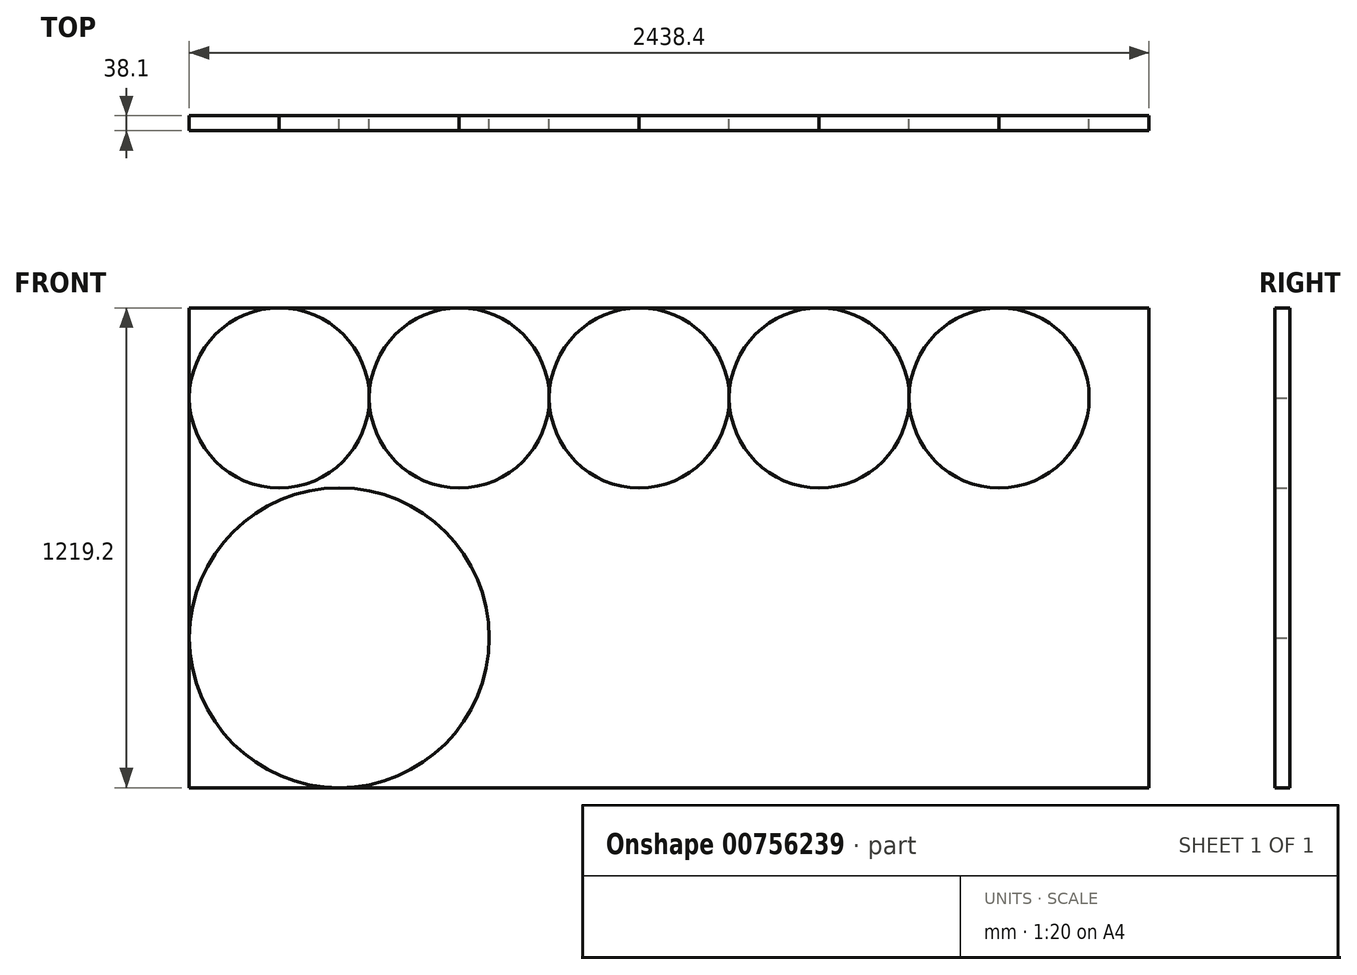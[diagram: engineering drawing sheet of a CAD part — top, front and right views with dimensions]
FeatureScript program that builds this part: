
annotation { "Feature Type Name" : "Feature", "Feature Type Description" : "" }
export const myFeature = defineFeature(function(context is Context, id is Id, definition is map)
    precondition{}
    {
        {
            var Q0;
            Q0=qCreatedBy(makeId("Front.planeOp"),FACE);
            var sketch = newSketch(context, id + "F0", { "sketchPlane" : qUnion([Q0])});
            skLineSegment(sketch, "E0.bottom", {"start": v(-1219.2, 609.6) * mm, "end": v(1219.2, 609.6) * mm});
            skLineSegment(sketch, "E0.top", {"start": v(-1219.2, -609.6) * mm, "end": v(1219.2, -609.6) * mm});
            skLineSegment(sketch, "E0.left", {"start": v(-1219.2, 609.6) * mm, "end": v(-1219.2, -609.6) * mm});
            skLineSegment(sketch, "E0.right", {"start": v(1219.2, 609.6) * mm, "end": v(1219.2, -609.6) * mm});
            skPoint(sketch, "E0.middle", {"position": v(0, 0) * mm});
            skCircle(sketch, "E1", {"center": v(-990.6, 381) * mm, "radius": 228.6 * mm});
            skCircle(sketch, "E2", {"center": v(-533.4, 381) * mm, "radius": 228.6 * mm});
            skCircle(sketch, "E3", {"center": v(-76.2, 381) * mm, "radius": 228.6 * mm});
            skCircle(sketch, "E4", {"center": v(381, 381) * mm, "radius": 228.6 * mm});
            skCircle(sketch, "E5", {"center": v(838.2, 381) * mm, "radius": 228.6 * mm});
            skCircle(sketch, "E6", {"center": v(-838.2, -228.6) * mm, "radius": 381 * mm});
            skSolve(sketch);
        }
        {
            var Q0;
            {var subQ0=sQuery(id+"F0.wireOp",EDGE,"E0.left");var subQ1=sQuery(id+"F0.wireOp",EDGE,"E0.bottom");var subQ2=makeQuery(id+"F0.imprint","INTERSECT",VERTEX,{"derivedFrom":[subQ1,subQ0]});Q0=makeQuery(id+"F0.imprint","IMPRINT",FACE,{"disambiguationData":[TD([[makeQuery(id+"F0.imprint","IMPRINT",EDGE,{"disambiguationData":[TD([[subQ2,-1.0]])],"derivedFrom":subQ1}),-1.0]])]});}
            var Q1;
            {var subQ0=sQuery(id+"F0.wireOp",EDGE,"E1");var subQ1=sQuery(id+"F0.wireOp",EDGE,"E0.bottom");var subQ2=makeQuery(id+"F0.imprint","INTERSECT",VERTEX,{"derivedFrom":[subQ1,subQ0]});Q1=makeQuery(id+"F0.imprint","IMPRINT",FACE,{"disambiguationData":[TD([[makeQuery(id+"F0.imprint","IMPRINT",EDGE,{"disambiguationData":[TD([[subQ2,-1.0]])],"derivedFrom":subQ1}),-1.0]])]});}
            var Q2;
            {var subQ0=sQuery(id+"F0.wireOp",EDGE,"E2");var subQ1=sQuery(id+"F0.wireOp",EDGE,"E0.bottom");var subQ2=makeQuery(id+"F0.imprint","INTERSECT",VERTEX,{"derivedFrom":[subQ1,subQ0]});Q2=makeQuery(id+"F0.imprint","IMPRINT",FACE,{"disambiguationData":[TD([[makeQuery(id+"F0.imprint","IMPRINT",EDGE,{"disambiguationData":[TD([[subQ2,-1.0]])],"derivedFrom":subQ1}),-1.0]])]});}
            var Q3;
            {var subQ0=sQuery(id+"F0.wireOp",EDGE,"E3");var subQ1=sQuery(id+"F0.wireOp",EDGE,"E0.bottom");var subQ2=makeQuery(id+"F0.imprint","INTERSECT",VERTEX,{"derivedFrom":[subQ1,subQ0]});Q3=makeQuery(id+"F0.imprint","IMPRINT",FACE,{"disambiguationData":[TD([[makeQuery(id+"F0.imprint","IMPRINT",EDGE,{"disambiguationData":[TD([[subQ2,-1.0]])],"derivedFrom":subQ1}),-1.0]])]});}
            var Q4;
            {var subQ0=sQuery(id+"F0.wireOp",EDGE,"E4");var subQ1=sQuery(id+"F0.wireOp",EDGE,"E0.bottom");var subQ2=makeQuery(id+"F0.imprint","INTERSECT",VERTEX,{"derivedFrom":[subQ1,subQ0]});Q4=makeQuery(id+"F0.imprint","IMPRINT",FACE,{"disambiguationData":[TD([[makeQuery(id+"F0.imprint","IMPRINT",EDGE,{"disambiguationData":[TD([[subQ2,-1.0]])],"derivedFrom":subQ1}),-1.0]])]});}
            var Q5;
            {var subQ0=sQuery(id+"F0.wireOp",EDGE,"E0.right");Q5=makeQuery(id+"F0.imprint","IMPRINT",FACE,{"disambiguationData":[TD([[makeQuery(id+"F0.imprint","IMPRINT",EDGE,{"derivedFrom":subQ0}),-1.0]])]});}
            var Q6;
            {var subQ0=sQuery(id+"F0.wireOp",EDGE,"E0.left");var subQ1=sQuery(id+"F0.wireOp",EDGE,"E0.top");var subQ2=makeQuery(id+"F0.imprint","INTERSECT",VERTEX,{"derivedFrom":[subQ1,subQ0]});Q6=makeQuery(id+"F0.imprint","IMPRINT",FACE,{"disambiguationData":[TD([[makeQuery(id+"F0.imprint","IMPRINT",EDGE,{"disambiguationData":[TD([[subQ2,-1.0]])],"derivedFrom":subQ1}),1.0]])]});}
            extrude(context, id + "F1", {"entities" : qUnion([Q0, Q1, Q2, Q3, Q4, Q5, Q6]), "endBound" : BoundingType.SYMMETRIC, "depth" : 38.1 * mm, "offsetDistance" : 25.4 * mm});
        }
    });
